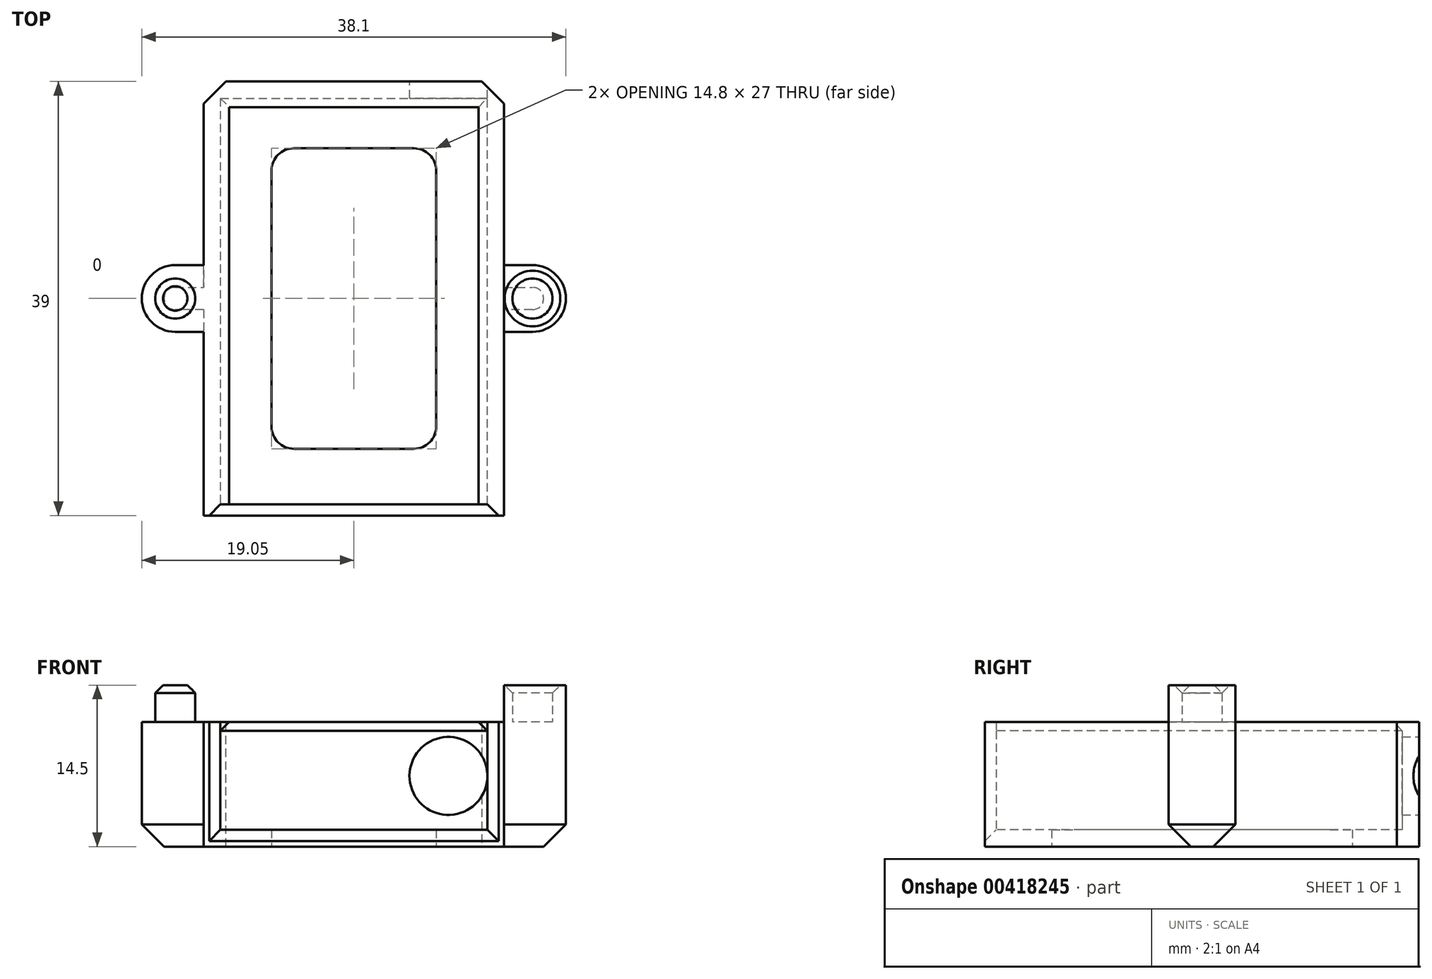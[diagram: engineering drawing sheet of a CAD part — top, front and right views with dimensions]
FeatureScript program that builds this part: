
annotation { "Feature Type Name" : "Feature", "Feature Type Description" : "" }
export const myFeature = defineFeature(function(context is Context, id is Id, definition is map)
    precondition{}
    {
        {
            var Q0;
            Q0=qCreatedBy(makeId("Top.planeOp"),FACE);
            var sketch = newSketch(context, id + "F0", { "sketchPlane" : qUnion([Q0])});
            skCircle(sketch, "E0", {"center": v(-16.05, 0) * mm, "radius": 1.8 * mm});
            skCircle(sketch, "E1.MirrorC", {"center": v(16.05, 0) * mm, "radius": 1.8 * mm});
            skArc(sketch, "E2", {"start": v(-16.05, 3) * mm, "mid": v(-19.05, 0) * mm, "end": v(-16.05, -3) * mm});
            skLineSegment(sketch, "E3", {"start": v(-16.05, 3) * mm, "end": v(-13.5, 3) * mm});
            skLineSegment(sketch, "E4.MirrorCS", {"start": v(-16.05, -3) * mm, "end": v(-13.5, -3) * mm});
            skLineSegment(sketch, "E5.MirrorCS", {"start": v(16.05, -3) * mm, "end": v(13.5, -3) * mm});
            skArc(sketch, "E6.MirrorCS", {"start": v(16.05, 3) * mm, "mid": v(19.05, 0) * mm, "end": v(16.05, -3) * mm});
            skPoint(sketch, "E7", {"position": v(0, 0) * mm});
            skLineSegment(sketch, "E8", {"start": v(16.05, 3) * mm, "end": v(13.5, 3) * mm});
            skLineSegment(sketch, "E9", {"start": v(-12, 19.5) * mm, "end": v(-12, -19.5) * mm});
            skLineSegment(sketch, "E10.MirrorCS", {"start": v(12, 19.5) * mm, "end": v(12, -19.5) * mm});
            skLineSegment(sketch, "E11", {"start": v(-13.5, 19.5) * mm, "end": v(-13.5, -19.5) * mm});
            skLineSegment(sketch, "E12.MirrorCS", {"start": v(13.5, 19.5) * mm, "end": v(13.5, -19.5) * mm});
            skLineSegment(sketch, "E13", {"start": v(-13.5, 19.5) * mm, "end": v(13.5, 19.5) * mm});
            skLineSegment(sketch, "E14.MirrorCS", {"start": v(-13.5, -19.5) * mm, "end": v(13.5, -19.5) * mm});
            skPoint(sketch, "E15.orphan", {"position": v(-13.5, 17.5) * mm});
            skPoint(sketch, "E16.orphan", {"position": v(-12, 17.5) * mm});
            skPoint(sketch, "E17.orphan", {"position": v(12, 17.5) * mm});
            skPoint(sketch, "E18.orphan", {"position": v(13.5, 17.5) * mm});
            skPoint(sketch, "E19.orphan", {"position": v(12, -17.5) * mm});
            skPoint(sketch, "E20.orphan", {"position": v(13.5, -17.5) * mm});
            skPoint(sketch, "E21.orphan", {"position": v(-13.5, -17.5) * mm});
            skPoint(sketch, "E22.orphan", {"position": v(-12, -17.5) * mm});
            skLineSegment(sketch, "E23", {"start": v(-12, 18) * mm, "end": v(12, 18) * mm});
            skLineSegment(sketch, "E24.bottom", {"start": v(7.4, 13.5) * mm, "end": v(-7.4, 13.5) * mm});
            skLineSegment(sketch, "E24.top", {"start": v(7.4, -13.5) * mm, "end": v(-7.4, -13.5) * mm});
            skLineSegment(sketch, "E24.left", {"start": v(7.4, 13.5) * mm, "end": v(7.4, -13.5) * mm});
            skLineSegment(sketch, "E24.right", {"start": v(-7.4, 13.5) * mm, "end": v(-7.4, -13.5) * mm});
            skSolve(sketch);
        }
        {
            var Q0;
            {var subQ0=sQuery(id+"F0.wireOp",EDGE,"E9");Q0=makeQuery(id+"F0.imprint","IMPRINT",FACE,{"disambiguationData":[TD([[makeQuery(id+"F0.imprint","IMPRINT",EDGE,{"derivedFrom":subQ0}),1.0]])]});}
            extrude(context, id + "F1", {"entities" : qUnion([Q0]), "depth" : 1.5 * mm});
        }
        {
            var Q0;
            Q0=makeQuery(id+"F0.imprint","IMPRINT",FACE,{"disambiguationData":[TD([[makeQuery(id+"F0.imprint","IMPRINT",EDGE,{"derivedFrom":sQuery(id+"F0.wireOp",EDGE,"E0")}),-1.0]])]});
            var Q1;
            Q1=makeQuery(id+"F0.imprint","IMPRINT",FACE,{"disambiguationData":[TD([[makeQuery(id+"F0.imprint","IMPRINT",EDGE,{"derivedFrom":sQuery(id+"F0.wireOp",EDGE,"E0")}),1.0]])]});
            var Q2;
            {var subQ7=sQuery(id+"F0.wireOp",EDGE,"E9");Q2=makeQuery(id+"F0.imprint","IMPRINT",FACE,{"disambiguationData":[TD([[makeQuery(id+"F0.imprint","IMPRINT",EDGE,{"derivedFrom":subQ7}),-1.0]])]});}
            var Q3;
            Q3=makeQuery(id+"F0.imprint","IMPRINT",FACE,{"disambiguationData":[TD([[makeQuery(id+"F0.imprint","IMPRINT",EDGE,{"derivedFrom":sQuery(id+"F0.wireOp",EDGE,"E1.MirrorC")}),1.0]])]});
            var Q4;
            Q4=makeQuery(id+"F0.imprint","IMPRINT",FACE,{"disambiguationData":[TD([[makeQuery(id+"F0.imprint","IMPRINT",EDGE,{"derivedFrom":sQuery(id+"F0.wireOp",EDGE,"E1.MirrorC")}),-1.0]])]});
            var Q5;
            {var subQ7=sQuery(id+"F0.wireOp",EDGE,"E10.MirrorCS");Q5=makeQuery(id+"F0.imprint","IMPRINT",FACE,{"disambiguationData":[TD([[makeQuery(id+"F0.imprint","IMPRINT",EDGE,{"derivedFrom":subQ7}),1.0]])]});}
            extrude(context, id + "F2", {"entities" : qUnion([Q0, Q1, Q2, Q3, Q4, Q5]), "operationType" : NewBodyOperationType.ADD, "depth" : (9.7 + 1.5) * mm});
        }
        {
            var Q0;
            Q0=makeQuery(id+"F0.imprint","IMPRINT",FACE,{"disambiguationData":[TD([[makeQuery(id+"F0.imprint","IMPRINT",EDGE,{"derivedFrom":sQuery(id+"F0.wireOp",EDGE,"E0")}),1.0]])]});
            var Q1;
            Q1=makeQuery(id+"F0.imprint","IMPRINT",FACE,{"disambiguationData":[TD([[makeQuery(id+"F0.imprint","IMPRINT",EDGE,{"derivedFrom":sQuery(id+"F0.wireOp",EDGE,"E1.MirrorC")}),-1.0]])]});
            extrude(context, id + "F3", {"entities" : qUnion([Q0, Q1]), "operationType" : NewBodyOperationType.ADD, "depth" : 14.5 * mm});
        }
        {
            var Q0;
            Q0=makeQuery(id+"F3.opExtrude","CAP_EDGE",EDGE,{"disambiguationData":[OSD([sQuery(id+"F0.wireOp",EDGE,"E1.MirrorC")])],"isStart":false});
            var Q1;
            Q1=makeQuery(id+"F3.opExtrude","CAP_EDGE",EDGE,{"disambiguationData":[OSD([sQuery(id+"F0.wireOp",EDGE,"E0")])],"isStart":false});
            chamfer(context, id + "F4", {"entities" : qUnion([Q0, Q1]), "width" : 0.7 * mm, "tangentPropagation" : true});
        }
        {
            var Q0;
            {var subQ3=sQuery(id+"F0.wireOp",EDGE,"E23");Q0=makeQuery(id+"F0.imprint","IMPRINT",FACE,{"disambiguationData":[TD([[makeQuery(id+"F0.imprint","IMPRINT",EDGE,{"derivedFrom":subQ3}),1.0]])]});}
            var Q1;
            Q1=makeQuery(id+"F2.opExtrude","CAP_FACE",FACE,{"disambiguationData":[OSD([sQuery(id+"F0.wireOp",EDGE,"E2"),sQuery(id+"F0.wireOp",EDGE,"E3"),sQuery(id+"F0.wireOp",EDGE,"E4.MirrorCS"),sQuery(id+"F0.wireOp",EDGE,"E9"),sQuery(id+"F0.wireOp",EDGE,"E11"),sQuery(id+"F0.wireOp",EDGE,"E13"),sQuery(id+"F0.wireOp",EDGE,"E14.MirrorCS")])],"isStart":false});
            extrude(context, id + "F5", {"entities" : qUnion([Q0]), "operationType" : NewBodyOperationType.ADD, "endBound" : BoundingType.UP_TO_SURFACE, "endBoundEntityFace" : qUnion([Q1]), "depth" : 25 * mm});
        }
        {
            var Q0;
            {var subQ5=sQuery(id+"F0.wireOp",EDGE,"E23");Q0=makeQuery(id+"F0.imprint","IMPRINT",FACE,{"disambiguationData":[TD([[makeQuery(id+"F0.imprint","IMPRINT",EDGE,{"derivedFrom":subQ5}),-1.0]])]});}
            extrude(context, id + "F6", {"entities" : qUnion([Q0]), "operationType" : NewBodyOperationType.ADD, "depth" : 1.5 * mm});
        }
        {
            var Q0;
            Q0=makeQuery(id+"F2.opExtrude","SWEPT_EDGE",EDGE,{"disambiguationData":[OSD([sQuery(id+"F0.wireOp",EDGE,"E10.MirrorCS"),sQuery(id+"F0.wireOp",EDGE,"E14.MirrorCS")])]});
            var Q1;
            Q1=makeQuery(id+"F6.opExtrude","CAP_EDGE",EDGE,{"disambiguationData":[OSD([sQuery(id+"F0.wireOp",EDGE,"E14.MirrorCS")])],"isStart":false});
            var Q2;
            Q2=makeQuery(id+"F2.opExtrude","SWEPT_EDGE",EDGE,{"disambiguationData":[OSD([sQuery(id+"F0.wireOp",EDGE,"E9"),sQuery(id+"F0.wireOp",EDGE,"E14.MirrorCS")])]});
            chamfer(context, id + "F7", {"entities" : qUnion([Q0, Q1, Q2]), "width" : 1 * mm, "tangentPropagation" : true});
        }
        {
            var Q0;
            Q0=makeQuery(id+"F6.opExtrude","SWEPT_EDGE",EDGE,{"disambiguationData":[OSD([sQuery(id+"F0.wireOp",EDGE,"E24.bottom"),sQuery(id+"F0.wireOp",EDGE,"E24.left")])]});
            var Q1;
            Q1=makeQuery(id+"F6.opExtrude","SWEPT_EDGE",EDGE,{"disambiguationData":[OSD([sQuery(id+"F0.wireOp",EDGE,"E24.bottom"),sQuery(id+"F0.wireOp",EDGE,"E24.right")])]});
            var Q2;
            Q2=makeQuery(id+"F6.opExtrude","SWEPT_EDGE",EDGE,{"disambiguationData":[OSD([sQuery(id+"F0.wireOp",EDGE,"E24.top"),sQuery(id+"F0.wireOp",EDGE,"E24.left")])]});
            var Q3;
            Q3=makeQuery(id+"F6.opExtrude","SWEPT_EDGE",EDGE,{"disambiguationData":[OSD([sQuery(id+"F0.wireOp",EDGE,"E24.top"),sQuery(id+"F0.wireOp",EDGE,"E24.right")])]});
            fillet(context, id + "F8", {"entities" : qUnion([Q0, Q1, Q2, Q3]), "radius" : 2 * mm, "tangentPropagation" : true, "allowEdgeOverflow" : false});
        }
        {
            var Q0;
            {var subQ0=sQuery(id+"F0.wireOp",EDGE,"E13");Q0=makeQuery(id+"F5.boolean.opBoolean","MERGE",FACE,{"derivedFrom":[makeQuery(id+"F2.boolean.opBoolean","MERGE",FACE,{"derivedFrom":[makeQuery(id+"F1.opExtrude","SWEPT_FACE",FACE,{"disambiguationData":[OSD([subQ0])]}),makeQuery(id+"F2.opExtrude","SWEPT_FACE",FACE,{"disambiguationData":[OSD([subQ0]),TDD([makeQuery(id+"F0.imprint","IMPRINT",EDGE,{"disambiguationData":[TD([[makeQuery(id+"F0.imprint","INTERSECT",VERTEX,{"derivedFrom":[sQuery(id+"F0.wireOp",EDGE,"E9"),subQ0]}),1.0]])],"derivedFrom":subQ0})])]}),makeQuery(id+"F2.opExtrude","SWEPT_FACE",FACE,{"disambiguationData":[OSD([subQ0]),TDD([makeQuery(id+"F0.imprint","IMPRINT",EDGE,{"disambiguationData":[TD([[makeQuery(id+"F0.imprint","INTERSECT",VERTEX,{"derivedFrom":[sQuery(id+"F0.wireOp",EDGE,"E10.MirrorCS"),subQ0]}),-1.0]])],"derivedFrom":subQ0})])]})]}),makeQuery(id+"F5.opExtrude","SWEPT_FACE",FACE,{"disambiguationData":[OSD([subQ0])]})]});}
            var sketch = newSketch(context, id + "F9", { "sketchPlane" : qUnion([Q0])});
            skPoint(sketch, "E25.centerSnap0", {"position": v(-13.5, 5.6) * mm});
            skCircle(sketch, "E26", {"center": v(-8.5, 6.35) * mm, "radius": 3.5 * mm});
            skSolve(sketch);
        }
        {
            var Q0;
            Q0=makeQuery(id+"F2.opExtrude","SWEPT_EDGE",EDGE,{"disambiguationData":[OSD([sQuery(id+"F0.wireOp",EDGE,"E12.MirrorCS"),sQuery(id+"F0.wireOp",EDGE,"E13")])]});
            var Q1;
            Q1=makeQuery(id+"F2.opExtrude","SWEPT_EDGE",EDGE,{"disambiguationData":[OSD([sQuery(id+"F0.wireOp",EDGE,"E11"),sQuery(id+"F0.wireOp",EDGE,"E13")])]});
            var Q2;
            Q2=makeQuery(id+"F2.opExtrude","CAP_EDGE",EDGE,{"disambiguationData":[OSD([sQuery(id+"F0.wireOp",EDGE,"E6.MirrorCS")])],"isStart":true});
            var Q3;
            Q3=makeQuery(id+"F2.opExtrude","CAP_EDGE",EDGE,{"disambiguationData":[OSD([sQuery(id+"F0.wireOp",EDGE,"E2")])],"isStart":true});
            chamfer(context, id + "F10", {"entities" : qUnion([Q0, Q1, Q2, Q3]), "width" : 2 * mm, "tangentPropagation" : true});
        }
        {
            var Q0;
            Q0=makeQuery(id+"F2.opExtrude","SWEPT_FACE",FACE,{"disambiguationData":[OSD([sQuery(id+"F0.wireOp",EDGE,"E9")])]});
            var sketch = newSketch(context, id + "F11", { "sketchPlane" : qUnion([Q0])});
            skLineSegment(sketch, "E27", {"start": v(-18.5, 11.2) * mm, "end": v(18, 11.2) * mm});
            skLineSegment(sketch, "E28", {"start": v(18, 11.2) * mm, "end": v(18, 10.4) * mm});
            skLineSegment(sketch, "E29", {"start": v(18, 10.4) * mm, "end": v(-18.5, 10.4) * mm});
            skLineSegment(sketch, "E30", {"start": v(-18.5, 10.4) * mm, "end": v(-18.5, 11.2) * mm});
            skSolve(sketch);
        }
        {
            var Q0;
            Q0=makeQuery(id+"F2.opExtrude","SWEPT_FACE",FACE,{"disambiguationData":[OSD([sQuery(id+"F0.wireOp",EDGE,"E10.MirrorCS")])]});
            var sketch = newSketch(context, id + "F12", { "sketchPlane" : qUnion([Q0])});
            skLineSegment(sketch, "E31", {"start": v(-18, 11.2) * mm, "end": v(18.5, 11.2) * mm});
            skLineSegment(sketch, "E32", {"start": v(18.5, 11.2) * mm, "end": v(18.5, 10.4) * mm});
            skLineSegment(sketch, "E33", {"start": v(18.5, 10.4) * mm, "end": v(-18, 10.4) * mm});
            skLineSegment(sketch, "E34", {"start": v(-18, 10.4) * mm, "end": v(-18, 11.2) * mm});
            skSolve(sketch);
        }
        {
            var Q0;
            Q0=makeQuery(id+"F12.imprint","IMPRINT",FACE,{"disambiguationData":[TD([[makeQuery(id+"F12.imprint","IMPRINT",EDGE,{"derivedFrom":sQuery(id+"F12.wireOp",EDGE,"E31")}),-1.0]])]});
            extrude(context, id + "F13", {"entities" : qUnion([Q0]), "operationType" : NewBodyOperationType.ADD, "depth" : 0.8 * mm});
        }
        {
            var Q0;
            Q0=makeQuery(id+"F11.imprint","IMPRINT",FACE,{"disambiguationData":[TD([[makeQuery(id+"F11.imprint","IMPRINT",EDGE,{"derivedFrom":sQuery(id+"F11.wireOp",EDGE,"E27")}),1.0]])]});
            extrude(context, id + "F14", {"entities" : qUnion([Q0]), "operationType" : NewBodyOperationType.ADD, "depth" : 0.8 * mm});
        }
        {
            var Q0;
            Q0=makeQuery(id+"F14.opExtrude","CAP_EDGE",EDGE,{"disambiguationData":[OSD([sQuery(id+"F11.wireOp",EDGE,"E29")])],"isStart":false});
            var Q1;
            Q1=makeQuery(id+"F13.opExtrude","CAP_EDGE",EDGE,{"disambiguationData":[OSD([sQuery(id+"F12.wireOp",EDGE,"E33")])],"isStart":false});
            var Q2;
            Q2=makeQuery(id+"F6.opExtrude","CAP_EDGE",EDGE,{"disambiguationData":[OSD([sQuery(id+"F0.wireOp",EDGE,"E9")])],"isStart":false});
            var Q3;
            Q3=makeQuery(id+"F6.opExtrude","CAP_EDGE",EDGE,{"disambiguationData":[OSD([sQuery(id+"F0.wireOp",EDGE,"E10.MirrorCS")])],"isStart":false});
            var Q4;
            Q4=makeQuery(id+"F6.opExtrude","CAP_EDGE",EDGE,{"disambiguationData":[OSD([sQuery(id+"F0.wireOp",EDGE,"E23")])],"isStart":false});
            chamfer(context, id + "F15", {"entities" : qUnion([Q0, Q1, Q2, Q3, Q4]), "width" : 0.8 * mm, "tangentPropagation" : true});
        }
        {
            var Q0;
            Q0=makeQuery(id+"F9.imprint","IMPRINT",FACE,{"disambiguationData":[TD([[makeQuery(id+"F9.imprint","IMPRINT",EDGE,{"derivedFrom":sQuery(id+"F9.wireOp",EDGE,"E26")}),1.0]])]});
            extrude(context, id + "F16", {"entities" : qUnion([Q0]), "operationType" : NewBodyOperationType.REMOVE, "oppositeDirection" : true, "depth" : 1.5 * mm});
        }
        {
            var Q0;
            {var subQ0=sQuery(id+"F0.wireOp",EDGE,"E23");Q0=makeQuery(id+"F5.boolean.opBoolean","MERGE",FACE,{"derivedFrom":[makeQuery(id+"F1.opExtrude","SWEPT_FACE",FACE,{"disambiguationData":[OSD([subQ0])]}),makeQuery(id+"F5.opExtrude","SWEPT_FACE",FACE,{"disambiguationData":[OSD([subQ0])]})]});}
            var sketch = newSketch(context, id + "F17", { "sketchPlane" : qUnion([Q0])});
            skLineSegment(sketch, "E35", {"start": v(12, 10.4) * mm, "end": v(-12, 10.4) * mm});
            skSolve(sketch);
        }
        {
            var Q0;
            Q0=makeQuery(id+"F17.imprint","IMPRINT",FACE,{"disambiguationData":[TD([[makeQuery(id+"F17.imprint","IMPRINT",EDGE,{"derivedFrom":sQuery(id+"F17.wireOp",EDGE,"E35")}),-1.0]])]});
            extrude(context, id + "F18", {"entities" : qUnion([Q0]), "operationType" : NewBodyOperationType.ADD, "depth" : 0.8 * mm});
        }
        {
            var Q0;
            Q0=makeQuery(id+"F18.opExtrude","CAP_EDGE",EDGE,{"disambiguationData":[OSD([sQuery(id+"F17.wireOp",EDGE,"E35")])],"isStart":false});
            chamfer(context, id + "F19", {"entities" : qUnion([Q0]), "width" : 0.8 * mm, "tangentPropagation" : true});
        }
        {
            var Q0;
            Q0=makeQuery(id+"F1.opExtrude","SWEPT_BODY",BODY,{"disambiguationData":[OSD([sQuery(id+"F0.wireOp",EDGE,"E9"),sQuery(id+"F0.wireOp",EDGE,"E10.MirrorCS"),sQuery(id+"F0.wireOp",EDGE,"E13"),sQuery(id+"F0.wireOp",EDGE,"E23")])]});
            transform(context, id + "F20", {"entities" : qUnion([Q0]), "transformType" : TransformType.TRANSLATION_3D, "dx" : 0 * mm, "dy" : 0 * mm, "dz" : 0 * mm, "makeCopy" : true});
        }
    });
